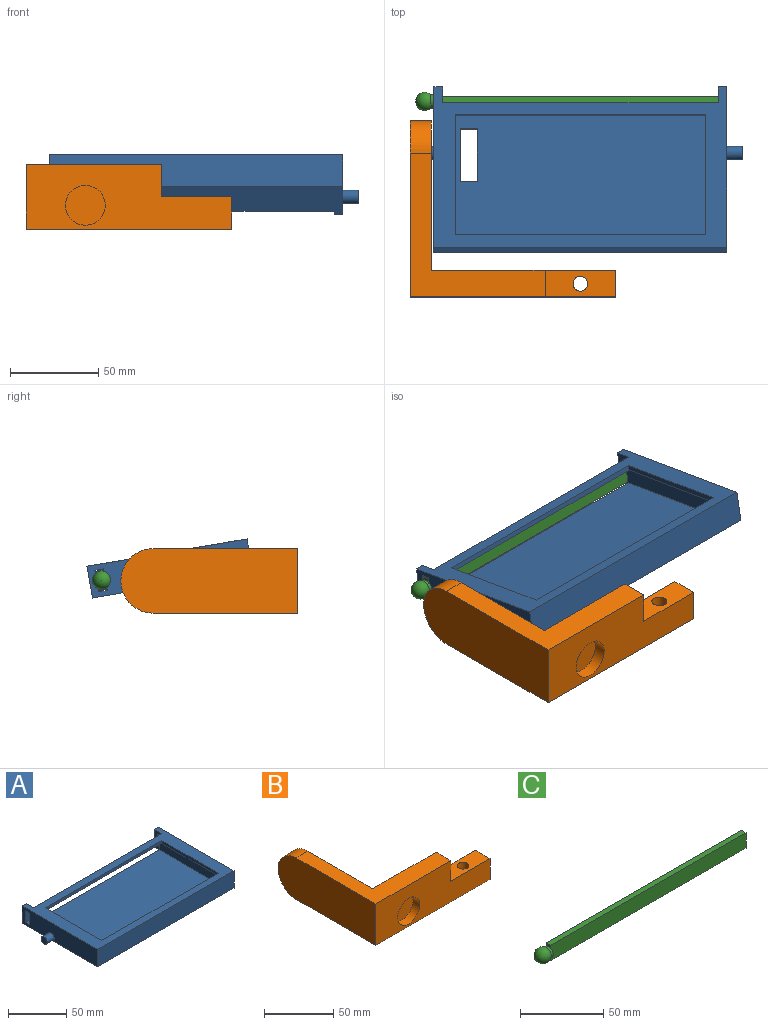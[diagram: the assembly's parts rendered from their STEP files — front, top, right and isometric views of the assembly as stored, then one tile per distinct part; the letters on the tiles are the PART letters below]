
ASSEMBLY  parts=3 mates=2
PART A: 33 faces, bbox 183x92x18.2 mm
  f0: plane 166x18.2mm, normal (0,1,0), area 1131.2mm2, adj f2,f4,f5,f10,f11,f16,f17,f18
  f1: plane 166x18.2mm, normal (0,-1,0), area 3021.2mm2, adj f5,f16,f22,f27
  f2: plane 80x12.2mm, normal (-1,0,0), area 976mm2, adj f0,f3,f10,f11
  f3: plane 150x12.2mm, normal (0,1,0), area 1830mm2, adj f2,f4,f10,f11
  f4: plane 80x12.2mm, normal (1,0,0), area 976mm2, adj f0,f3,f10,f11
  f5: plane 166x92mm, normal (0,0,-1), area 13570.1mm2, adj f0,f1,f6,f7,f8,f9,f17,f20
  f6: plane 9.8x3mm, normal (0,-1,0), area 29.4mm2, adj f5,f7,f9,f10
  f7: plane 30.4x3mm, normal (-1,0,0), area 91.2mm2, adj f5,f6,f8,f10
  f8: plane 9.8x3mm, normal (0,1,0), area 29.4mm2, adj f5,f7,f9,f10
  f9: plane 30.4x3mm, normal (1,0,0), area 91.2mm2, adj f5,f6,f8,f10
  f10: plane 150x80mm, normal (0,0,1), area 11702.1mm2, adj f0,f2,f3,f4,f6,f7,f8,f9
  f11: plane 150x80mm, normal (0,0,-1), area 2202mm2, adj f0,f2,f3,f4,f12,f13,f14,f15
  f12: plane 69x3mm, normal (1,0,0), area 207mm2, adj f11,f13,f15,f16
  f13: plane 142x3mm, normal (0,-1,0), area 426mm2, adj f11,f12,f14,f16
  f14: plane 69x3mm, normal (-1,0,0), area 207mm2, adj f11,f13,f15,f16
  f15: plane 142x3mm, normal (0,1,0), area 426mm2, adj f11,f12,f14,f16
  f16: plane 166x92mm, normal (0,0,1), area 4070mm2, adj f0,f1,f12,f13,f14,f15,f17,f20
  f17: plane 18.2x9mm, normal (1,0,0), area 102.8mm2, adj f0,f5,f16,f18,f19,f20,f21
  f18: plane 5x5mm, normal (0,0,1), area 25mm2, adj f0,f17,f19,f22
  f19: plane 12.2x5mm, normal (0,-1,0), area 61mm2, adj f17,f18,f21,f22
  f20: plane 18.2x5mm, normal (0,1,0), area 91mm2, adj f5,f16,f17,f22
  f21: plane 5x5mm, normal (0,0,-1), area 25mm2, adj f0,f17,f19,f22
  f22: plane 92x18.2mm, normal (-1,0,0), area 1569.2mm2, adj f0,f1,f5,f16,f18,f19,f20,f21
  f23: plane 5x5mm, normal (0,0,1), area 25mm2, adj f0,f24,f27,f28
  f24: plane 12.2x5mm, normal (0,-1,0), area 61mm2, adj f23,f26,f27,f28
  f25: plane 18.2x5mm, normal (0,1,0), area 91mm2, adj f5,f16,f27,f28
  f26: plane 5x5mm, normal (0,0,-1), area 25mm2, adj f0,f24,f27,f28
  f27: plane 92x18.2mm, normal (1,0,0), area 1569.2mm2, adj f0,f1,f5,f16,f23,f24,f25,f26
  f28: plane 18.2x9mm, normal (-1,0,0), area 102.8mm2, adj f0,f5,f16,f23,f24,f25,f26
  f29: cylinder r=3.75mm len=8.5mm, axis (1,0,0), area 200.3mm2, adj f22,f30
  f30: plane 7.5x7.5mm, normal (-1,0,0), area 44.2mm2, adj f29
  f31: cylinder r=3.75mm len=8.5mm, axis (-1,0,0), area 200.3mm2, adj f27,f32
  f32: plane 7.5x7.5mm, normal (1,0,0), area 44.2mm2, adj f31
PART B: 15 faces, bbox 116.5x99.8x36.5 mm
  f0: plane 18.25x15mm, normal (1,0,0), area 273.8mm2, adj f2,f10,f11,f13
  f1: plane 18.25x15mm, normal (1,0,0), area 273.8mm2, adj f2,f10,f11,f14
  f2: plane 40x15mm, normal (0,0,1), area 544.6mm2, adj f0,f1,f10,f11,f12
  f3: plane 22.5x22.5mm, normal (1,0,0), area 397.6mm2, adj f5
  f4: plane 22.5x22.5mm, normal (0,-1,0), area 397.6mm2, adj f8
  f5: cylinder r=11.25mm len=22.5mm, axis (-1,0,0), area 494.8mm2, adj f3,f9
  f6: cylinder r=18.25mm len=36.5mm, axis (1,0,0), area 688mm2, adj f7,f9,f13,f14
  f7: plane 99.75x36.5mm, normal (-1,0,0), area 3497.9mm2, adj f6,f11,f13,f14
  f8: cylinder r=11.25mm len=22.5mm, axis (0,-1,0), area 494.8mm2, adj f4,f11
  f9: plane 84.75x36.5mm, normal (1,0,0), area 2552.8mm2, adj f5,f6,f10,f13,f14
  f10: plane 104.5x36.5mm, normal (0,1,0), area 3084.2mm2, adj f0,f1,f2,f9,f13,f14
  f11: plane 116.5x36.5mm, normal (0,-1,0), area 3124.6mm2, adj f0,f1,f2,f7,f8,f13,f14
  f12: cylinder r=4.2mm len=18.25mm, axis (0,0,1), area 481.6mm2, adj f2,f13
  f13: plane 116.5x81.5mm, normal (0,0,-1), area 2490.1mm2, adj f0,f6,f7,f9,f10,f11,f12
  f14: plane 81.5x76.5mm, normal (0,0,1), area 1945.5mm2, adj f1,f6,f7,f9,f10,f11
PART C: 11 faces, bbox 176.3x10.3x11.2 mm
  f0: plane 4x2.3mm, normal (-1,0,0), area 7.7mm2, adj f2,f4,f5,f9
  f1: plane 11.2x4mm, normal (1,0,0), area 44.8mm2, adj f2,f4,f5,f6
  f2: plane 166x4mm, normal (0,0,1), area 664mm2, adj f0,f1,f4,f5
  f3: plane 4x2.3mm, normal (-1,0,0), area 7.7mm2, adj f4,f5,f6,f9
  f4: plane 166x11.2mm, normal (0,-1,0), area 1859.2mm2, adj f0,f1,f2,f3,f6,f7
  f5: plane 166x11.2mm, normal (0,1,0), area 1859.2mm2, adj f0,f1,f2,f3,f6,f8
  f6: plane 166x4mm, normal (0,0,-1), area 664mm2, adj f1,f3,f4,f5
  f7: plane 6.59x1.86mm, normal (1,0,0), area 8.6mm2, adj f4,f9
  f8: plane 6.59x1.86mm, normal (1,0,0), area 8.6mm2, adj f5,f9
  f9: cylinder r=3.86mm len=7.71mm, axis (1,0,0), area 42.6mm2, adj f0,f3,f7,f8,f10
  f10: sphere r=5.16mm, area 278mm2, adj f9
PLACE A rot(axis=(-1,0,0),9.7deg) t=(0,-0.16,3.64)mm
PLACE B t=(0,0.26,0)mm fixed
PLACE C rot(axis=(-1,0,0),9.7deg) t=(0,-0.41,3.68)mm
MATE revolute B.f5 <-> A.f29  axis (1,0,0) through (-91.5,15.26,4.8)mm
MATE fastened A.f22 <-> C.f8  axis (-1,0,0) through (-83,47.21,4.75)mm
